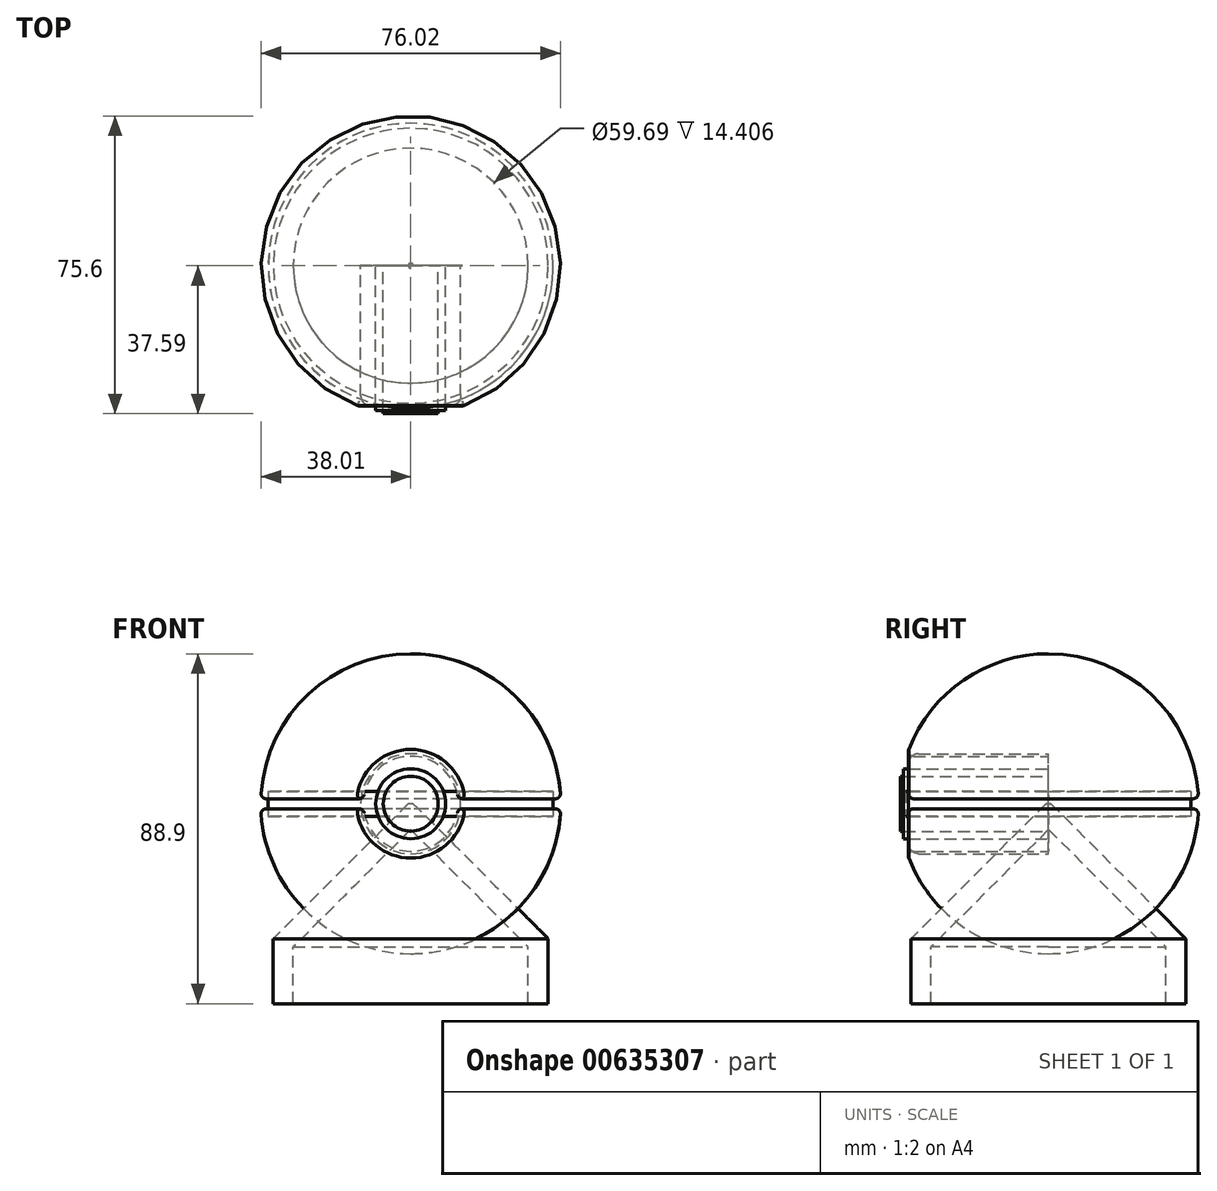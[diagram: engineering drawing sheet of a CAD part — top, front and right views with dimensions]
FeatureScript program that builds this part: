
annotation { "Feature Type Name" : "Feature", "Feature Type Description" : "" }
export const myFeature = defineFeature(function(context is Context, id is Id, definition is map)
    precondition{}
    {
        {
            var Q0;
            Q0=qCreatedBy(makeId("Top.planeOp"),FACE);
            var sketch = newSketch(context, id + "F0", { "sketchPlane" : qUnion([Q0])});
            skCircle(sketch, "E0", {"center": v(0, 0) * mm, "radius": 38.1 * mm});
            skSolve(sketch);
        }
        {
            var Q0;
            Q0=makeQuery(id+"F0.imprint","IMPRINT",FACE,{"disambiguationData":[TD([[makeQuery(id+"F0.imprint","IMPRINT",EDGE,{"derivedFrom":sQuery(id+"F0.wireOp",EDGE,"E0")}),1.0]])]});
            extrude(context, id + "F1", {"entities" : qUnion([Q0]), "endBound" : BoundingType.SYMMETRIC, "depth" : 76.2 * mm, "offsetDistance" : 25.4 * mm});
        }
        {
            var Q0;
            Q0=makeQuery(id+"F1.opExtrude","CAP_FACE",FACE,{"disambiguationData":[OSD([sQuery(id+"F0.wireOp",EDGE,"E0")])],"isStart":false});
            var Q1;
            Q1=makeQuery(id+"F1.opExtrude","CAP_EDGE",EDGE,{"disambiguationData":[OSD([sQuery(id+"F0.wireOp",EDGE,"E0")])],"isStart":true});
            fillet(context, id + "F2", {"entities" : qUnion([Q0, Q1]), "radius" : 38.1 * mm, "tangentPropagation" : true, "allowEdgeOverflow" : false});
        }
        {
            var Q0;
            Q0=qCreatedBy(makeId("Front.planeOp"),FACE);
            var sketch = newSketch(context, id + "F3", { "sketchPlane" : qUnion([Q0])});
            skCircle(sketch, "E1", {"center": v(0, 0) * mm, "radius": 12.07 * mm});
            skSolve(sketch);
        }
        {
            var Q0;
            Q0 = qSketchRegion(id + "F3", true);
            extrude(context, id + "F4", {"entities" : qUnion([Q0]), "operationType" : NewBodyOperationType.REMOVE, "depth" : 40.64 * mm, "offsetDistance" : 25.4 * mm});
        }
        {
            var Q0;
            Q0=qCreatedBy(makeId("Top.planeOp"),FACE);
            var sketch = newSketch(context, id + "F5", { "sketchPlane" : qUnion([Q0])});
            skCircle(sketch, "E2", {"center": v(0, 0) * mm, "radius": 38.1 * mm});
            skSolve(sketch);
        }
        {
            var Q0;
            Q0 = qSketchRegion(id + "F5", true);
            extrude(context, id + "F6", {"entities" : qUnion([Q0]), "operationType" : NewBodyOperationType.REMOVE, "endBound" : BoundingType.SYMMETRIC, "depth" : 2.54 * mm, "offsetDistance" : 25.4 * mm});
        }
        {
            var Q0;
            Q0=qCreatedBy(makeId("Top.planeOp"),FACE);
            var sketch = newSketch(context, id + "F7", { "sketchPlane" : qUnion([Q0])});
            skCircle(sketch, "E3", {"center": v(0, 0) * mm, "radius": 36.2 * mm});
            skSolve(sketch);
        }
        {
            var Q0;
            Q0 = qSketchRegion(id + "F7", true);
            extrude(context, id + "F8", {"entities" : qUnion([Q0]), "endBound" : BoundingType.SYMMETRIC, "depth" : 6.35 * mm, "offsetDistance" : 25.4 * mm});
        }
        {
            var Q0;
            Q0=qCreatedBy(makeId("Front.planeOp"),FACE);
            var sketch = newSketch(context, id + "F9", { "sketchPlane" : qUnion([Q0])});
            skCircle(sketch, "E4", {"center": v(0, 0) * mm, "radius": 12.7 * mm});
            skSolve(sketch);
        }
        {
            var Q0;
            Q0 = qSketchRegion(id + "F9", true);
            extrude(context, id + "F10", {"entities" : qUnion([Q0]), "depth" : 35.56 * mm, "offsetDistance" : 25.4 * mm});
        }
        {
            var Q0;
            Q0=makeQuery(id+"F10.opExtrude","CAP_EDGE",EDGE,{"disambiguationData":[OSD([sQuery(id+"F9.wireOp",EDGE,"E4")])],"isStart":false});
            fillet(context, id + "F11", {"entities" : qUnion([Q0]), "radius" : 2.54 * mm, "tangentPropagation" : true, "allowEdgeOverflow" : false});
        }
        {
            var Q0;
            Q0=qCreatedBy(makeId("Front.planeOp"),FACE);
            var sketch = newSketch(context, id + "F12", { "sketchPlane" : qUnion([Q0])});
            skCircle(sketch, "E5", {"center": v(0, 0) * mm, "radius": 8.9 * mm});
            skSolve(sketch);
        }
        {
            var Q0;
            Q0 = qSketchRegion(id + "F12", true);
            extrude(context, id + "F13", {"entities" : qUnion([Q0]), "depth" : 36.83 * mm, "offsetDistance" : 25.4 * mm});
        }
        {
            var Q0;
            Q0=qCreatedBy(makeId("Front.planeOp"),FACE);
            var sketch = newSketch(context, id + "F14", { "sketchPlane" : qUnion([Q0])});
            skCircle(sketch, "E6", {"center": v(0, 0) * mm, "radius": 6.99 * mm});
            skSolve(sketch);
        }
        {
            var Q0;
            Q0 = qSketchRegion(id + "F14", true);
            extrude(context, id + "F15", {"entities" : qUnion([Q0]), "depth" : 37.6 * mm, "offsetDistance" : 25.4 * mm});
        }
        {
            var Q0;
            Q0=makeQuery(id+"F6.boolean.opBoolean","INTERSECT",EDGE,{"derivedFrom":[makeQuery(id+"F2.opFillet","BLEND_FACE",FACE,{"disambiguationData":[OSD([sQuery(id+"F0.wireOp",EDGE,"E0")])]}),makeQuery(id+"F6.opExtrude","CAP_FACE",FACE,{"disambiguationData":[OSD([sQuery(id+"F5.wireOp",EDGE,"E2")])],"isStart":false})]});
            var Q1;
            Q1=makeQuery(id+"F6.boolean.opBoolean","INTERSECT",EDGE,{"derivedFrom":[makeQuery(id+"F2.opFillet","BLEND_FACE",FACE,{"disambiguationData":[OSD([sQuery(id+"F0.wireOp",EDGE,"E0")])]}),makeQuery(id+"F6.opExtrude","CAP_FACE",FACE,{"disambiguationData":[OSD([sQuery(id+"F5.wireOp",EDGE,"E2")])],"isStart":true})]});
            fillet(context, id + "F16", {"entities" : qUnion([Q0, Q1]), "radius" : 1.27 * mm, "tangentPropagation" : true, "allowEdgeOverflow" : false});
        }
        {
            var Q0;
            {var subQ0=makeQuery(id+"F2.opFillet","BLEND_FACE",FACE,{"disambiguationData":[OSD([sQuery(id+"F0.wireOp",EDGE,"E0")])]});var subQ1=makeQuery(id+"F4.opExtrude","SWEPT_FACE",FACE,{"disambiguationData":[OSD([sQuery(id+"F3.wireOp",EDGE,"E1")])]});Q0=makeQuery(id+"F6.boolean.opBoolean","SPLIT",EDGE,{"disambiguationData":[TD([makeQuery(id+"F6.opExtrude","CAP_FACE",FACE,{"disambiguationData":[OSD([sQuery(id+"F5.wireOp",EDGE,"E2")])],"isStart":false})])],"derivedFrom":makeQuery(id+"F4.boolean.opBoolean","INTERSECT",EDGE,{"derivedFrom":[subQ0,subQ1]})});}
            var Q1;
            {var subQ0=makeQuery(id+"F2.opFillet","BLEND_FACE",FACE,{"disambiguationData":[OSD([sQuery(id+"F0.wireOp",EDGE,"E0")])]});var subQ1=makeQuery(id+"F4.opExtrude","SWEPT_FACE",FACE,{"disambiguationData":[OSD([sQuery(id+"F3.wireOp",EDGE,"E1")])]});Q1=makeQuery(id+"F6.boolean.opBoolean","SPLIT",EDGE,{"disambiguationData":[TD([makeQuery(id+"F6.opExtrude","CAP_FACE",FACE,{"disambiguationData":[OSD([sQuery(id+"F5.wireOp",EDGE,"E2")])],"isStart":true})])],"derivedFrom":makeQuery(id+"F4.boolean.opBoolean","INTERSECT",EDGE,{"derivedFrom":[subQ0,subQ1]})});}
            fillet(context, id + "F17", {"entities" : qUnion([Q0, Q1]), "radius" : 1.27 * mm, "tangentPropagation" : true, "allowEdgeOverflow" : false});
        }
        {
            var Q0;
            Q0=qCreatedBy(makeId("Top.planeOp"),FACE);
            var sketch = newSketch(context, id + "F18", { "sketchPlane" : qUnion([Q0])});
            skCircle(sketch, "E7", {"center": v(0, 0) * mm, "radius": 34.93 * mm});
            skSolve(sketch);
        }
        {
            var Q0;
            Q0 = qSketchRegion(id + "F18", true);
            extrude(context, id + "F19", {"entities" : qUnion([Q0]), "oppositeDirection" : true, "depth" : 50.8 * mm, "offsetDistance" : 25.4 * mm});
        }
        {
            var Q0;
            Q0=makeQuery(id+"F19.opExtrude","CAP_EDGE",EDGE,{"disambiguationData":[OSD([sQuery(id+"F18.wireOp",EDGE,"E7")])],"isStart":true});
            chamfer(context, id + "F20", {"entities" : qUnion([Q0]), "width" : 34.3 * mm, "tangentPropagation" : true});
        }
        {
            var Q0;
            Q0=makeQuery(id+"F19.opExtrude","CAP_FACE",FACE,{"disambiguationData":[OSD([sQuery(id+"F18.wireOp",EDGE,"E7")])],"isStart":false});
            shell(context, id + "F21", {"entities" : qUnion([Q0]), "thickness" : 5.08 * mm});
        }
    });
